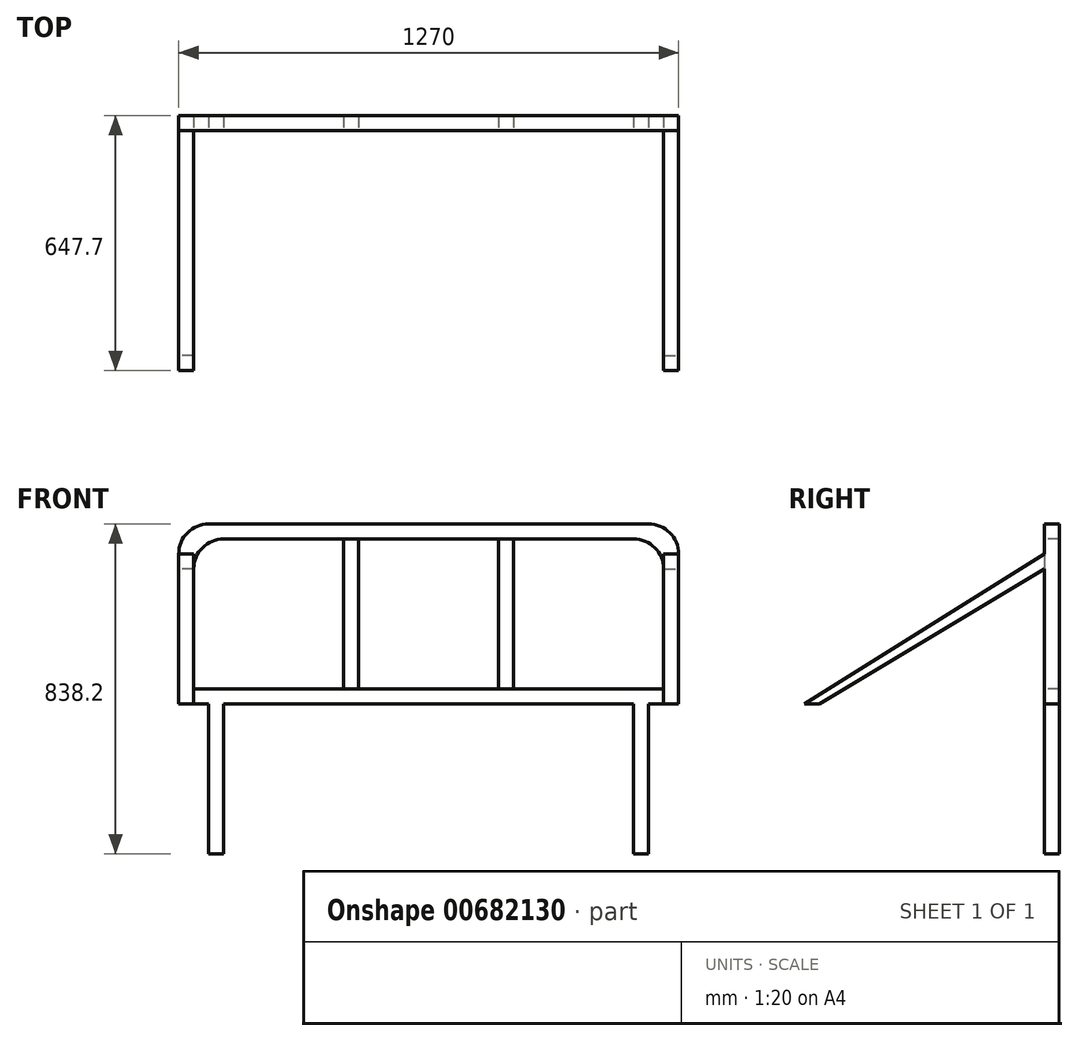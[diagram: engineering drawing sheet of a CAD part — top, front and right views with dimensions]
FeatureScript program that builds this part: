
annotation { "Feature Type Name" : "Feature", "Feature Type Description" : "" }
export const myFeature = defineFeature(function(context is Context, id is Id, definition is map)
    precondition{}
    {
        {
            var Q0;
            Q0=qCreatedBy(makeId("Front.planeOp"),FACE);
            var sketch = newSketch(context, id + "F0", { "sketchPlane" : qUnion([Q0])});
            skLineSegment(sketch, "E0.bottom", {"start": v(-548.73, 197.9) * mm, "end": v(568.87, 197.9) * mm});
            skLineSegment(sketch, "E0.top", {"start": v(-624.93, -259.3) * mm, "end": v(645.07, -259.3) * mm});
            skLineSegment(sketch, "E0.left", {"start": v(-624.93, 121.7) * mm, "end": v(-624.93, -259.3) * mm});
            skLineSegment(sketch, "E0.right", {"start": v(645.07, 121.7) * mm, "end": v(645.07, -259.3) * mm});
            skPoint(sketch, "E1.visualSharp", {"position": v(-624.93, 197.9) * mm});
            skArc(sketch, "E1.filletArc", {"start": v(-548.73, 197.9) * mm, "mid": v(-602.6, 175.58) * mm, "end": v(-624.93, 121.7) * mm});
            skPoint(sketch, "E2.visualSharp", {"position": v(645.07, 197.9) * mm});
            skArc(sketch, "E2.filletArc", {"start": v(645.07, 121.7) * mm, "mid": v(622.76, 175.58) * mm, "end": v(568.87, 197.9) * mm});
            skSolve(sketch);
        }
        {
            var Q0;
            Q0 = qSketchRegion(id + "F0", true);
            extrude(context, id + "F1", {"entities" : qUnion([Q0]), "depth" : 38.1 * mm, "offsetDistance" : 25.4 * mm});
        }
        {
            var Q0;
            Q0=makeQuery(id+"F1.opExtrude","CAP_FACE",FACE,{"disambiguationData":[OSD([sQuery(id+"F0.wireOp",EDGE,"E0.bottom"),sQuery(id+"F0.wireOp",EDGE,"E0.top"),sQuery(id+"F0.wireOp",EDGE,"E0.left"),sQuery(id+"F0.wireOp",EDGE,"E0.right"),sQuery(id+"F0.wireOp",EDGE,"E1.filletArc"),sQuery(id+"F0.wireOp",EDGE,"E2.filletArc")])],"isStart":false});
            var sketch = newSketch(context, id + "F2", { "sketchPlane" : qUnion([Q0])});
            skLineSegment(sketch, "E3.bottom", {"start": v(-510.63, 159.8) * mm, "end": v(530.77, 159.8) * mm});
            skLineSegment(sketch, "E3.top", {"start": v(-586.83, -221.2) * mm, "end": v(606.97, -221.2) * mm});
            skLineSegment(sketch, "E3.left", {"start": v(-586.83, 83.6) * mm, "end": v(-586.83, -221.2) * mm});
            skLineSegment(sketch, "E3.right", {"start": v(606.97, 83.6) * mm, "end": v(606.97, -221.2) * mm});
            skPoint(sketch, "E4.visualSharp", {"position": v(-586.83, 159.8) * mm});
            skArc(sketch, "E4.filletArc", {"start": v(-510.63, 159.8) * mm, "mid": v(-564.5, 137.48) * mm, "end": v(-586.83, 83.6) * mm});
            skPoint(sketch, "E5.visualSharp", {"position": v(606.97, 159.8) * mm});
            skArc(sketch, "E5.filletArc", {"start": v(606.97, 83.6) * mm, "mid": v(584.66, 137.48) * mm, "end": v(530.77, 159.8) * mm});
            skSolve(sketch);
        }
        {
            var Q0;
            Q0 = qSketchRegion(id + "F2", true);
            extrude(context, id + "F3", {"entities" : qUnion([Q0]), "operationType" : NewBodyOperationType.REMOVE, "oppositeDirection" : true, "depth" : 38.1 * mm, "offsetDistance" : 25.4 * mm});
        }
        {
            var Q0;
            Q0=makeQuery(id+"F1.opExtrude","CAP_FACE",FACE,{"disambiguationData":[OSD([sQuery(id+"F0.wireOp",EDGE,"E0.bottom"),sQuery(id+"F0.wireOp",EDGE,"E0.top"),sQuery(id+"F0.wireOp",EDGE,"E0.left"),sQuery(id+"F0.wireOp",EDGE,"E0.right"),sQuery(id+"F0.wireOp",EDGE,"E1.filletArc"),sQuery(id+"F0.wireOp",EDGE,"E2.filletArc")])],"isStart":false});
            var sketch = newSketch(context, id + "F4", { "sketchPlane" : qUnion([Q0])});
            skLineSegment(sketch, "E6.left", {"start": v(-205.83, 159.8) * mm, "end": v(-205.83, -221.2) * mm});
            skLineSegment(sketch, "E6.right", {"start": v(-167.73, 159.8) * mm, "end": v(-167.73, -221.2) * mm});
            skLineSegment(sketch, "E7.bottom", {"start": v(187.87, 159.8) * mm, "end": v(225.97, 159.8) * mm});
            skLineSegment(sketch, "E7.top", {"start": v(187.87, -221.2) * mm, "end": v(225.97, -221.2) * mm});
            skLineSegment(sketch, "E7.left", {"start": v(187.87, 159.8) * mm, "end": v(187.87, -221.2) * mm});
            skLineSegment(sketch, "E7.right", {"start": v(225.97, 159.8) * mm, "end": v(225.97, -221.2) * mm});
            skLineSegment(sketch, "E8", {"start": v(-205.83, 159.8) * mm, "end": v(-167.73, 159.8) * mm});
            skLineSegment(sketch, "E9", {"start": v(-205.83, -221.2) * mm, "end": v(-167.73, -221.2) * mm});
            skSolve(sketch);
        }
        {
            var Q0;
            Q0 = qSketchRegion(id + "F4", true);
            extrude(context, id + "F5", {"entities" : qUnion([Q0]), "oppositeDirection" : true, "depth" : 38.1 * mm, "offsetDistance" : 25.4 * mm});
        }
        {
            var Q0;
            Q0=makeQuery(id+"F1.opExtrude","SWEPT_FACE",FACE,{"disambiguationData":[OSD([sQuery(id+"F0.wireOp",EDGE,"E0.right")])]});
            var sketch = newSketch(context, id + "F6", { "sketchPlane" : qUnion([Q0])});
            skLineSegment(sketch, "E10", {"start": v(-38.1, 121.7) * mm, "end": v(-38.1, -259.3) * mm});
            skLineSegment(sketch, "E11", {"start": v(-38.1, -259.3) * mm, "end": v(-647.7, -259.3) * mm});
            skLineSegment(sketch, "E12", {"start": v(-647.7, -259.3) * mm, "end": v(-38.1, 121.7) * mm});
            skSolve(sketch);
        }
        {
            var Q0;
            Q0 = qSketchRegion(id + "F6", true);
            extrude(context, id + "F7", {"entities" : qUnion([Q0]), "operationType" : NewBodyOperationType.ADD, "oppositeDirection" : true, "depth" : 38.1 * mm, "offsetDistance" : 25.4 * mm});
        }
        {
            var Q0;
            Q0=makeQuery(id+"F7.boolean.opBoolean","MERGE",FACE,{"derivedFrom":[makeQuery(id+"F1.opExtrude","SWEPT_FACE",FACE,{"disambiguationData":[OSD([sQuery(id+"F0.wireOp",EDGE,"E0.right")])]}),makeQuery(id+"F7.opExtrude","CAP_FACE",FACE,{"disambiguationData":[OSD([sQuery(id+"F6.wireOp",EDGE,"E10"),sQuery(id+"F6.wireOp",EDGE,"E11"),sQuery(id+"F6.wireOp",EDGE,"E12")])],"isStart":true})]});
            var sketch = newSketch(context, id + "F8", { "sketchPlane" : qUnion([Q0])});
            skLineSegment(sketch, "E13", {"start": v(-609.6, -259.3) * mm, "end": v(-38.1, -259.3) * mm});
            skLineSegment(sketch, "E14", {"start": v(-38.1, -259.3) * mm, "end": v(-38.1, 83.6) * mm});
            skLineSegment(sketch, "E15", {"start": v(-38.1, 83.6) * mm, "end": v(-609.6, -259.3) * mm});
            skSolve(sketch);
        }
        {
            var Q0;
            Q0 = qSketchRegion(id + "F8", true);
            extrude(context, id + "F9", {"entities" : qUnion([Q0]), "operationType" : NewBodyOperationType.REMOVE, "oppositeDirection" : true, "depth" : 38.1 * mm, "offsetDistance" : 25.4 * mm});
        }
        {
            var Q0;
            Q0=makeQuery(id+"F1.opExtrude","SWEPT_FACE",FACE,{"disambiguationData":[OSD([sQuery(id+"F0.wireOp",EDGE,"E0.left")])]});
            var sketch = newSketch(context, id + "F10", { "sketchPlane" : qUnion([Q0])});
            skLineSegment(sketch, "E16", {"start": v(38.1, 121.7) * mm, "end": v(38.1, -259.3) * mm});
            skLineSegment(sketch, "E17", {"start": v(38.1, -259.3) * mm, "end": v(647.7, -259.3) * mm});
            skLineSegment(sketch, "E18", {"start": v(647.7, -259.3) * mm, "end": v(38.1, 121.7) * mm});
            skSolve(sketch);
        }
        {
            var Q0;
            Q0 = qSketchRegion(id + "F10", true);
            extrude(context, id + "F11", {"entities" : qUnion([Q0]), "operationType" : NewBodyOperationType.ADD, "oppositeDirection" : true, "depth" : 38.1 * mm, "offsetDistance" : 25.4 * mm});
        }
        {
            var Q0;
            Q0=makeQuery(id+"F11.boolean.opBoolean","MERGE",FACE,{"derivedFrom":[makeQuery(id+"F1.opExtrude","SWEPT_FACE",FACE,{"disambiguationData":[OSD([sQuery(id+"F0.wireOp",EDGE,"E0.left")])]}),makeQuery(id+"F11.opExtrude","CAP_FACE",FACE,{"disambiguationData":[OSD([sQuery(id+"F10.wireOp",EDGE,"E16"),sQuery(id+"F10.wireOp",EDGE,"E17"),sQuery(id+"F10.wireOp",EDGE,"E18")])],"isStart":true})]});
            var sketch = newSketch(context, id + "F12", { "sketchPlane" : qUnion([Q0])});
            skLineSegment(sketch, "E19", {"start": v(38.1, -259.3) * mm, "end": v(38.1, 83.6) * mm});
            skLineSegment(sketch, "E20", {"start": v(38.1, 83.6) * mm, "end": v(609.6, -259.3) * mm});
            skLineSegment(sketch, "E21", {"start": v(609.6, -259.3) * mm, "end": v(38.1, -259.3) * mm});
            skSolve(sketch);
        }
        {
            var Q0;
            Q0 = qSketchRegion(id + "F12", true);
            extrude(context, id + "F13", {"entities" : qUnion([Q0]), "operationType" : NewBodyOperationType.REMOVE, "oppositeDirection" : true, "depth" : 38.1 * mm, "offsetDistance" : 25.4 * mm});
        }
        {
            var Q0;
            {var subQ3=sQuery(id+"F0.wireOp",EDGE,"E0.right");var subQ4=sQuery(id+"F0.wireOp",EDGE,"E0.top");var subQ5=makeQuery(id+"F1.opExtrude","CAP_FACE",FACE,{"disambiguationData":[OSD([sQuery(id+"F0.wireOp",EDGE,"E0.bottom"),subQ4,sQuery(id+"F0.wireOp",EDGE,"E0.left"),subQ3,sQuery(id+"F0.wireOp",EDGE,"E1.filletArc"),sQuery(id+"F0.wireOp",EDGE,"E2.filletArc")])],"isStart":false});var subQ7=makeQuery(id+"F9.opExtrude","SWEPT_FACE",FACE,{"disambiguationData":[OSD([sQuery(id+"F8.wireOp",EDGE,"E14")])]});Q0=makeQuery(id+"F13.boolean.opBoolean","MERGE",FACE,{"derivedFrom":[makeQuery(id+"F11.boolean.opBoolean","SPLIT",FACE,{"disambiguationData":[TD([makeQuery(id+"F1.opExtrude","SWEPT_FACE",FACE,{"disambiguationData":[OSD([subQ4])]})])],"derivedFrom":makeQuery(id+"F9.boolean.opBoolean","MERGE",FACE,{"derivedFrom":[subQ5,subQ7]})}),makeQuery(id+"F13.opExtrude","SWEPT_FACE",FACE,{"disambiguationData":[OSD([sQuery(id+"F12.wireOp",EDGE,"E19")])]})]});}
            var sketch = newSketch(context, id + "F14", { "sketchPlane" : qUnion([Q0])});
            skLineSegment(sketch, "E22.bottom", {"start": v(-548.73, -259.3) * mm, "end": v(-510.63, -259.3) * mm});
            skLineSegment(sketch, "E22.top", {"start": v(-548.73, -640.3) * mm, "end": v(-510.63, -640.3) * mm});
            skLineSegment(sketch, "E22.left", {"start": v(-548.73, -259.3) * mm, "end": v(-548.73, -640.3) * mm});
            skLineSegment(sketch, "E22.right", {"start": v(-510.63, -259.3) * mm, "end": v(-510.63, -640.3) * mm});
            skLineSegment(sketch, "E23.bottom", {"start": v(530.77, -259.3) * mm, "end": v(568.87, -259.3) * mm});
            skLineSegment(sketch, "E23.top", {"start": v(530.77, -640.3) * mm, "end": v(568.87, -640.3) * mm});
            skLineSegment(sketch, "E23.left", {"start": v(530.77, -259.3) * mm, "end": v(530.77, -640.3) * mm});
            skLineSegment(sketch, "E23.right", {"start": v(568.87, -259.3) * mm, "end": v(568.87, -640.3) * mm});
            skSolve(sketch);
        }
        {
            var Q0;
            Q0 = qSketchRegion(id + "F14", true);
            extrude(context, id + "F15", {"entities" : qUnion([Q0]), "operationType" : NewBodyOperationType.ADD, "oppositeDirection" : true, "depth" : 38.1 * mm, "offsetDistance" : 25.4 * mm});
        }
    });
